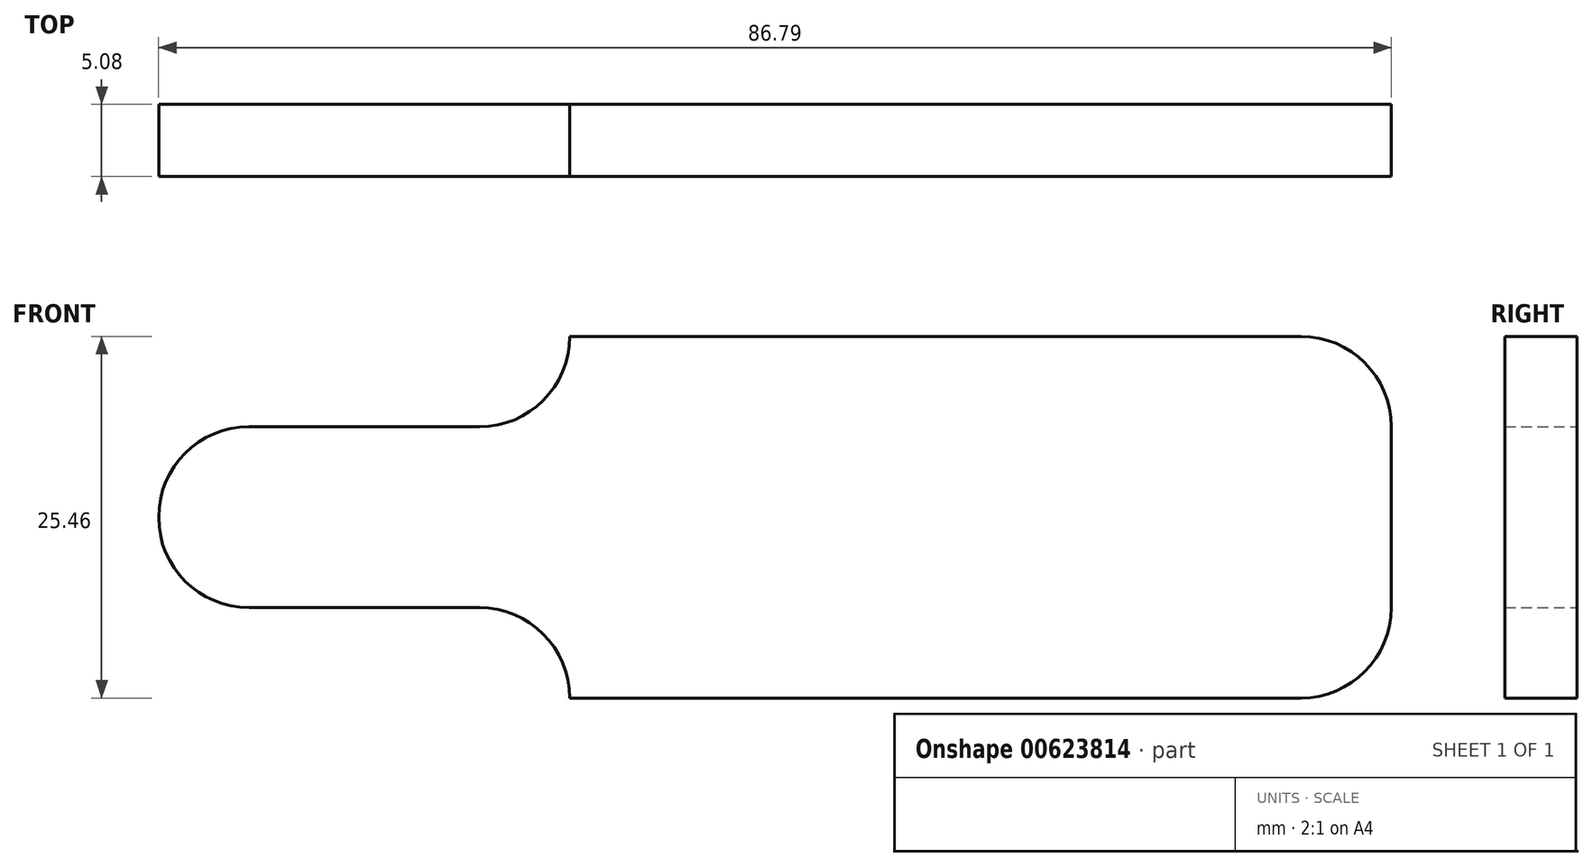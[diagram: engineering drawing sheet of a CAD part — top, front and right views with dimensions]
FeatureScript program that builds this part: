
annotation { "Feature Type Name" : "Feature", "Feature Type Description" : "" }
export const myFeature = defineFeature(function(context is Context, id is Id, definition is map)
    precondition{}
    {
        {
            var Q0;
            Q0=qCreatedBy(makeId("Front.planeOp"),FACE);
            var sketch = newSketch(context, id + "F0", { "sketchPlane" : qUnion([Q0])});
            skLineSegment(sketch, "E0", {"start": v(0, 12.71) * mm, "end": v(0, 12.73) * mm});
            skLineSegment(sketch, "E1", {"start": v(0, 12.73) * mm, "end": v(45.13, 12.73) * mm});
            skLineSegment(sketch, "E2", {"start": v(0, 0) * mm, "end": v(-28.93, 0) * mm});
            skLineSegment(sketch, "E3", {"start": v(-28.93, 0) * mm, "end": v(-28.93, 0.01) * mm});
            skPoint(sketch, "E3.endSnap0", {"position": v(0, 6.36) * mm});
            skLineSegment(sketch, "E4", {"start": v(-22.58, 6.36) * mm, "end": v(-6.35, 6.36) * mm});
            skPoint(sketch, "E5.newPointA", {"position": v(0, 0) * mm});
            skArc(sketch, "E5.filletArc", {"start": v(-6.35, 6.36) * mm, "mid": v(-1.86, 8.22) * mm, "end": v(0, 12.71) * mm});
            skLineSegment(sketch, "E6", {"start": v(57.86, 0) * mm, "end": v(0, 0) * mm});
            skLineSegment(sketch, "E7", {"start": v(57.86, 0) * mm, "end": v(57.86, 6.38) * mm});
            skLineSegment(sketch, "E8", {"start": v(51.5, 12.73) * mm, "end": v(45.13, 12.73) * mm});
            skPoint(sketch, "E9.visualSharp", {"position": v(57.86, 12.73) * mm});
            skArc(sketch, "E9.filletArc", {"start": v(57.86, 6.38) * mm, "mid": v(56, 10.87) * mm, "end": v(51.5, 12.73) * mm});
            skLineSegment(sketch, "E10.MirrorCS", {"start": v(0, -12.71) * mm, "end": v(0, -12.73) * mm});
            skLineSegment(sketch, "E11.MirrorCS", {"start": v(57.86, 0) * mm, "end": v(57.86, -6.38) * mm});
            skLineSegment(sketch, "E12.MirrorCS", {"start": v(51.5, -12.73) * mm, "end": v(45.13, -12.73) * mm});
            skLineSegment(sketch, "E13.MirrorCS", {"start": v(-28.93, 0) * mm, "end": v(-28.93, -0.01) * mm});
            skArc(sketch, "E14.MirrorCS", {"start": v(57.86, -6.38) * mm, "mid": v(56, -10.87) * mm, "end": v(51.5, -12.73) * mm});
            skArc(sketch, "E15.MirrorCS", {"start": v(-6.35, -6.36) * mm, "mid": v(-1.86, -8.22) * mm, "end": v(0, -12.71) * mm});
            skPoint(sketch, "E16.MirrorP", {"position": v(0, -6.36) * mm});
            skPoint(sketch, "E17.MirrorP", {"position": v(57.86, -12.73) * mm});
            skLineSegment(sketch, "E18.MirrorCS", {"start": v(-22.58, -6.36) * mm, "end": v(-6.35, -6.36) * mm});
            skLineSegment(sketch, "E19.MirrorCS", {"start": v(0, -12.73) * mm, "end": v(45.13, -12.73) * mm});
            skPoint(sketch, "E20.visualSharp", {"position": v(-28.93, 6.36) * mm});
            skArc(sketch, "E20.filletArc", {"start": v(-22.58, 6.36) * mm, "mid": v(-27.07, 4.5) * mm, "end": v(-28.93, 0.01) * mm});
            skPoint(sketch, "E21.visualSharp", {"position": v(-28.93, -6.36) * mm});
            skArc(sketch, "E21.filletArc", {"start": v(-28.93, -0.01) * mm, "mid": v(-27.07, -4.5) * mm, "end": v(-22.58, -6.36) * mm});
            skSolve(sketch);
        }
        {
            var Q0;
            Q0 = qSketchRegion(id + "F0", true);
            extrude(context, id + "F1", {"entities" : qUnion([Q0]), "depth" : 5.08 * mm, "offsetDistance" : 25.4 * mm});
        }
    });
